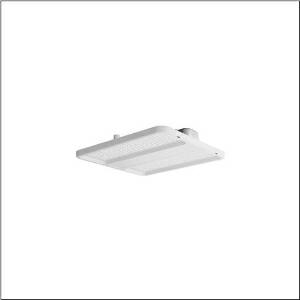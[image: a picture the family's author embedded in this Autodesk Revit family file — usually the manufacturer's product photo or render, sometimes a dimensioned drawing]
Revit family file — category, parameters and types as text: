
# Revit family: highbay_21_midi_52hn12da4fda
name_source: partatom
category: Lighting Fixtures
units: mm (PartAtom-declared; Revit-internal decimal feet)

## family parameters
Cut with Voids When Loaded = No
Host = Face
Light Source = No
Part Type = Normal
Room Calculation Point = No
Round Connector Dimension = Use Diameter
Shared = No

## types (1)
- --- (1 x LED, 2110 lm, 11.9 W, 4000K)
    Apparent Load = 12 VA
    CIE Flux Codes = 90 98 100 100 100
    Color Rendering = 80
    Color Temperature = 4000K
    Default Elevation = 1800 mm
    Description = high bay luminaire Highbay 21 midi; direct symmetric wide distribution, light control with lens of PMMA; UGR ≤ 22 (X = 4H | Y = 8H | S = 0.25H | reflection values 70/50/20); luminous flux: 14.000lm; light colour: 840, colour temperature: 4000K, MacAdam ≤ 3 SDCM (initial), colour rendering: CRI > 80; luminous efficacy: 194,2lm/W; rated service life: 75.000h (L80/B50) at AT= ta max; control: DALI 2; housing frame of high-performance plastic PA6, matt traffic white (RAL 9016); cover of PMMA; dimension (LxWxH): 474 x 442 x 72mm; luminaire connection: terminal, 5-pole, max. 2.5mm² (cable entry for one cable, Ø 8.5..16mm); mains connection: 230..240V, AC/DC 0/50..60Hz; connected load: 72,1W; protection rating (complete): IP66; insulation class (complete): insulation class I (protective earthing); protection symbol: D; impact resistance: IK08; halogen-free wiring; for central battery installations according to DIN EN 60598-2-22; LABS conformity tested according to VDMA 24364:2018-05; corresponds to IFS (International Featured Standards) requirements for safety and quality in the food industry; certification: CE, ENEC, VDE, UKCA; permissible operating ambient temperature: -40..+70°C (reducing of maximum allowable ambient temperature of 5°C with ceiling mounting); packaging unit: 1 piece; (delivery without accessories; please order mounting accessories separately)
    Height = 72 mm  [stored 0.23622 ft]
    Lamp = 1 x LED
    Lamp Light Flux = 2110 lm
    Lamp Power = 11.9 W
    Lamp count = 1
    Length = 474 mm
    Luminous efficacy = 177 lm/W
    Manufacturer = Siteco
    ModVariant = No
    Model = 52HN12DA4FDA
    Mounting Place = Ceiling
    Mounting Type = Pendant
    Number of Poles = 1
    OnlyDefault = Yes
    Power Factor = 1
    Product Name = Highbay 21 midi
    Product group = high bay luminaire
    ProductGroupID = 901
    Protection Class = Protection class I
    Protection Degree = IP 66
    RLX_Detail_Level = 1
    RLX_Emergency_Light_Flux = 0 lm
    RLX_Emergency_Type = 0
    RLX_Emergency_Type_DB = No
    RlxData = <blob elided: 17505 chars, md5=cd2e2412>
    Socket = socket
    Standby Power = 0 W
    System Light Flux = 2110 lm
    System Power = 12 W
    Type Comments = : DC mode (central or group accumulator) initial emergency light level
    Type Image = l_1363240.jpg
    URL = http://relux.com
    VarID = @adj_000569
    Voltage = 0 V
    Weight = 0.00 kg
    Width = 442 mm

note: [stored X ft] marks values corroborated as IEEE doubles in the binary element streams (Revit-internal decimal feet)

## geometry (parser evidence)
native form markers: Blend x4, Sweep x11
no freeform markers — native parametric forms only
